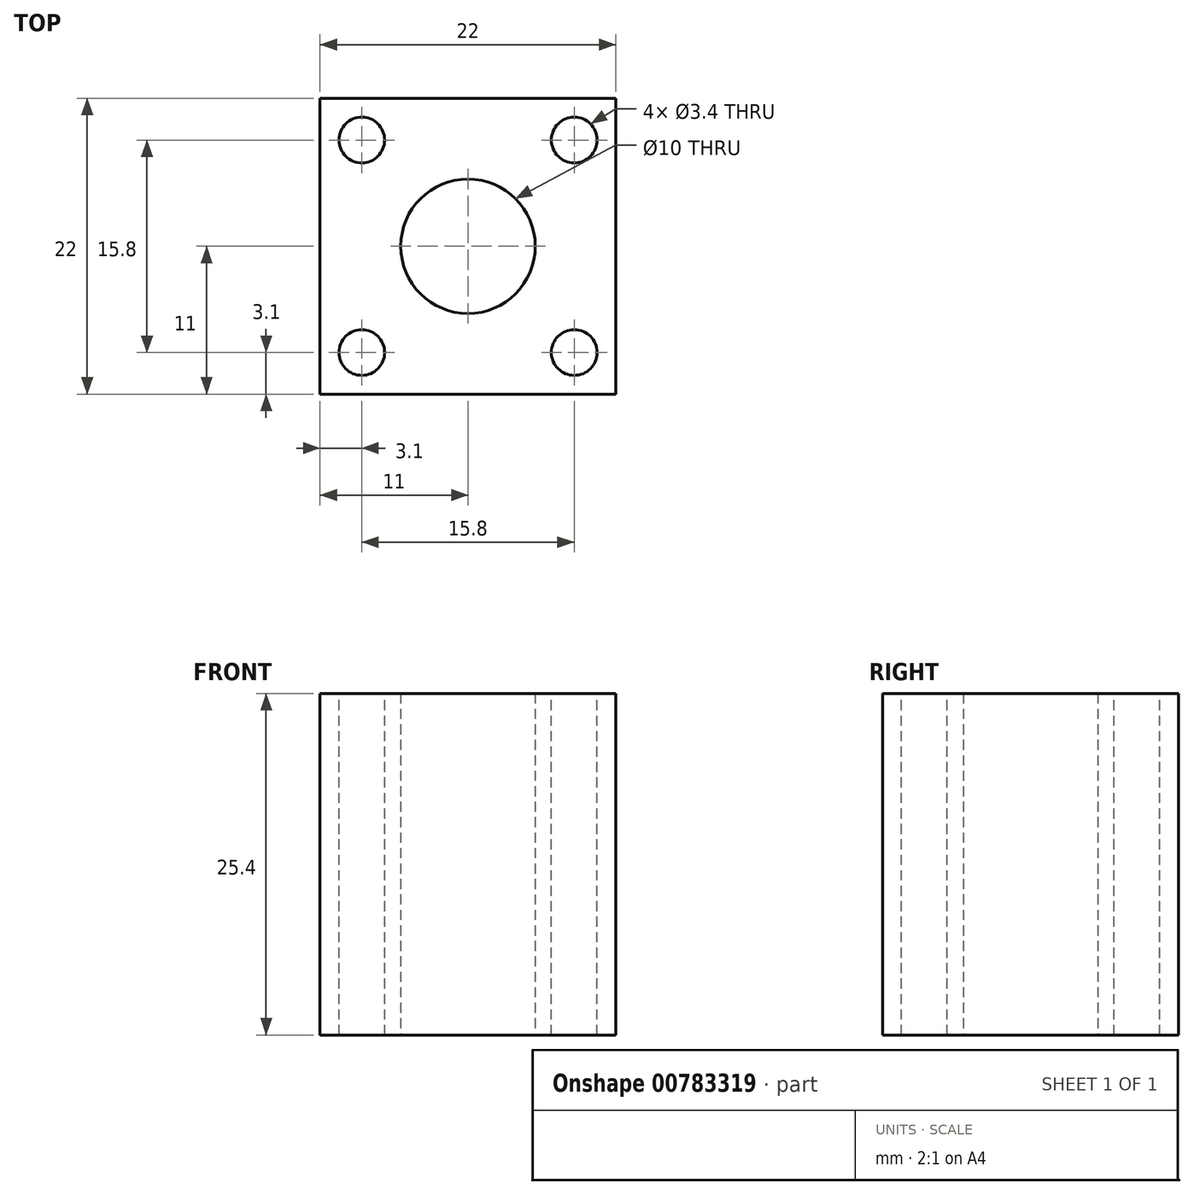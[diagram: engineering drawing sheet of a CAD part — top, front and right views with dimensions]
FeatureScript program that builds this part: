
annotation { "Feature Type Name" : "Feature", "Feature Type Description" : "" }
export const myFeature = defineFeature(function(context is Context, id is Id, definition is map)
    precondition{}
    {
        {
            var Q0;
            Q0=qCreatedBy(makeId("Top.planeOp"),FACE);
            var sketch = newSketch(context, id + "F0", { "sketchPlane" : qUnion([Q0])});
            skCircle(sketch, "E0", {"center": v(0, 0) * mm, "radius": 5 * mm});
            skLineSegment(sketch, "E1.bottom", {"start": v(11, -11) * mm, "end": v(-11, -11) * mm});
            skLineSegment(sketch, "E1.top", {"start": v(11, 11) * mm, "end": v(-11, 11) * mm});
            skLineSegment(sketch, "E1.left", {"start": v(11, -11) * mm, "end": v(11, 11) * mm});
            skLineSegment(sketch, "E1.right", {"start": v(-11, -11) * mm, "end": v(-11, 11) * mm});
            skLineSegment(sketch, "E2.bottom", {"start": v(-11, -11) * mm, "end": v(-7.9, -11) * mm});
            skLineSegment(sketch, "E2.left", {"start": v(-11, -11) * mm, "end": v(-11, -7.9) * mm});
            skPoint(sketch, "E3", {"position": v(-7.9, -6.9) * mm});
            skLineSegment(sketch, "E4.bottom", {"start": v(11, -11) * mm, "end": v(7.9, -11) * mm});
            skLineSegment(sketch, "E4.left", {"start": v(11, -11) * mm, "end": v(11, -7.9) * mm});
            skLineSegment(sketch, "E5.bottom", {"start": v(11, 11) * mm, "end": v(7.9, 11) * mm});
            skLineSegment(sketch, "E5.left", {"start": v(11, 11) * mm, "end": v(11, 7.9) * mm});
            skLineSegment(sketch, "E6.bottom", {"start": v(-11, 11) * mm, "end": v(-7.9, 11) * mm});
            skLineSegment(sketch, "E6.left", {"start": v(-11, 11) * mm, "end": v(-11, 7.9) * mm});
            skPoint(sketch, "E7", {"position": v(-7.9, 6.9) * mm});
            skPoint(sketch, "E8", {"position": v(7.9, 6.9) * mm});
            skPoint(sketch, "E9", {"position": v(7.9, -6.9) * mm});
            skSolve(sketch);
        }
        {
            var Q0;
            Q0=makeQuery(id+"F0.imprint","IMPRINT",FACE,{"disambiguationData":[TD([[makeQuery(id+"F0.imprint","IMPRINT",EDGE,{"derivedFrom":sQuery(id+"F0.wireOp",EDGE,"E0")}),-1.0]])]});
            extrude(context, id + "F1", {"entities" : qUnion([Q0]), "depth" : 25.4 * mm, "offsetDistance" : 25 * mm});
        }
        {
            var Q0;
            Q0=makeQuery(id+"F1.opExtrude","CAP_FACE",FACE,{"disambiguationData":[OSD([sQuery(id+"F0.wireOp",EDGE,"E0"),sQuery(id+"F0.wireOp",EDGE,"E1.bottom"),sQuery(id+"F0.wireOp",EDGE,"E1.top"),sQuery(id+"F0.wireOp",EDGE,"E1.left"),sQuery(id+"F0.wireOp",EDGE,"E1.right"),sQuery(id+"F0.wireOp",EDGE,"E2.bottom"),sQuery(id+"F0.wireOp",EDGE,"E2.left"),sQuery(id+"F0.wireOp",EDGE,"E4.bottom"),sQuery(id+"F0.wireOp",EDGE,"E4.left"),sQuery(id+"F0.wireOp",EDGE,"E5.bottom"),sQuery(id+"F0.wireOp",EDGE,"E5.left"),sQuery(id+"F0.wireOp",EDGE,"E6.bottom"),sQuery(id+"F0.wireOp",EDGE,"E6.left")])],"isStart":false});
            var sketch = newSketch(context, id + "F2", { "sketchPlane" : qUnion([Q0])});
            skLineSegment(sketch, "E10.bottom", {"start": v(-11, 11) * mm, "end": v(-7.9, 11) * mm});
            skLineSegment(sketch, "E10.top", {"start": v(-11, 7.9) * mm, "end": v(-7.9, 7.9) * mm});
            skLineSegment(sketch, "E10.left", {"start": v(-11, 11) * mm, "end": v(-11, 7.9) * mm});
            skLineSegment(sketch, "E10.right", {"start": v(-7.9, 11) * mm, "end": v(-7.9, 7.9) * mm});
            skLineSegment(sketch, "E11.bottom", {"start": v(-11, -11) * mm, "end": v(-7.9, -11) * mm});
            skLineSegment(sketch, "E11.top", {"start": v(-11, -7.9) * mm, "end": v(-7.9, -7.9) * mm});
            skLineSegment(sketch, "E11.left", {"start": v(-11, -11) * mm, "end": v(-11, -7.9) * mm});
            skLineSegment(sketch, "E11.right", {"start": v(-7.9, -11) * mm, "end": v(-7.9, -7.9) * mm});
            skLineSegment(sketch, "E12.bottom", {"start": v(11, 11) * mm, "end": v(7.9, 11) * mm});
            skLineSegment(sketch, "E12.top", {"start": v(11, 7.9) * mm, "end": v(7.9, 7.9) * mm});
            skLineSegment(sketch, "E12.left", {"start": v(11, 11) * mm, "end": v(11, 7.9) * mm});
            skLineSegment(sketch, "E12.right", {"start": v(7.9, 11) * mm, "end": v(7.9, 7.9) * mm});
            skLineSegment(sketch, "E13.bottom", {"start": v(11, -11) * mm, "end": v(7.9, -11) * mm});
            skLineSegment(sketch, "E13.top", {"start": v(11, -7.9) * mm, "end": v(7.9, -7.9) * mm});
            skLineSegment(sketch, "E13.left", {"start": v(11, -11) * mm, "end": v(11, -7.9) * mm});
            skLineSegment(sketch, "E13.right", {"start": v(7.9, -11) * mm, "end": v(7.9, -7.9) * mm});
            skPoint(sketch, "E14", {"position": v(-7.9, 7.9) * mm});
            skPoint(sketch, "E15", {"position": v(7.9, 7.9) * mm});
            skPoint(sketch, "E16", {"position": v(-7.9, -7.9) * mm});
            skPoint(sketch, "E17", {"position": v(7.9, -7.9) * mm});
            skSolve(sketch);
        }
        {
            var Q0;
            Q0=sQuery(id+"F2.wireOp",VERTEX,"E14");
            var Q1;
            Q1=sQuery(id+"F2.wireOp",VERTEX,"E16");
            var Q2;
            Q2=sQuery(id+"F2.wireOp",VERTEX,"E15");
            var Q3;
            Q3=sQuery(id+"F2.wireOp",VERTEX,"E17");
            var Q4;
            Q4=makeQuery(id+"F1.opExtrude","SWEPT_BODY",BODY,{"disambiguationData":[OSD([sQuery(id+"F0.wireOp",EDGE,"E0"),sQuery(id+"F0.wireOp",EDGE,"E1.bottom"),sQuery(id+"F0.wireOp",EDGE,"E1.top"),sQuery(id+"F0.wireOp",EDGE,"E1.left"),sQuery(id+"F0.wireOp",EDGE,"E1.right"),sQuery(id+"F0.wireOp",EDGE,"E2.bottom"),sQuery(id+"F0.wireOp",EDGE,"E2.left"),sQuery(id+"F0.wireOp",EDGE,"E4.bottom"),sQuery(id+"F0.wireOp",EDGE,"E4.left"),sQuery(id+"F0.wireOp",EDGE,"E5.bottom"),sQuery(id+"F0.wireOp",EDGE,"E5.left"),sQuery(id+"F0.wireOp",EDGE,"E6.bottom"),sQuery(id+"F0.wireOp",EDGE,"E6.left")])]});
            hole(context, id + "F3", {"style" : HoleStyle.SIMPLE, "endStyle" : HoleEndStyle.THROUGH, "holeDiameter" : 3.4 * mm, "majorDiameter" : 5 * mm, "isTappedThrough" : true, "tappedDepth" : 12 * mm, "tapClearance" : 3, "locations" : qUnion([Q0, Q1, Q2, Q3]), "scope" : qUnion([Q4])});
        }
    });
